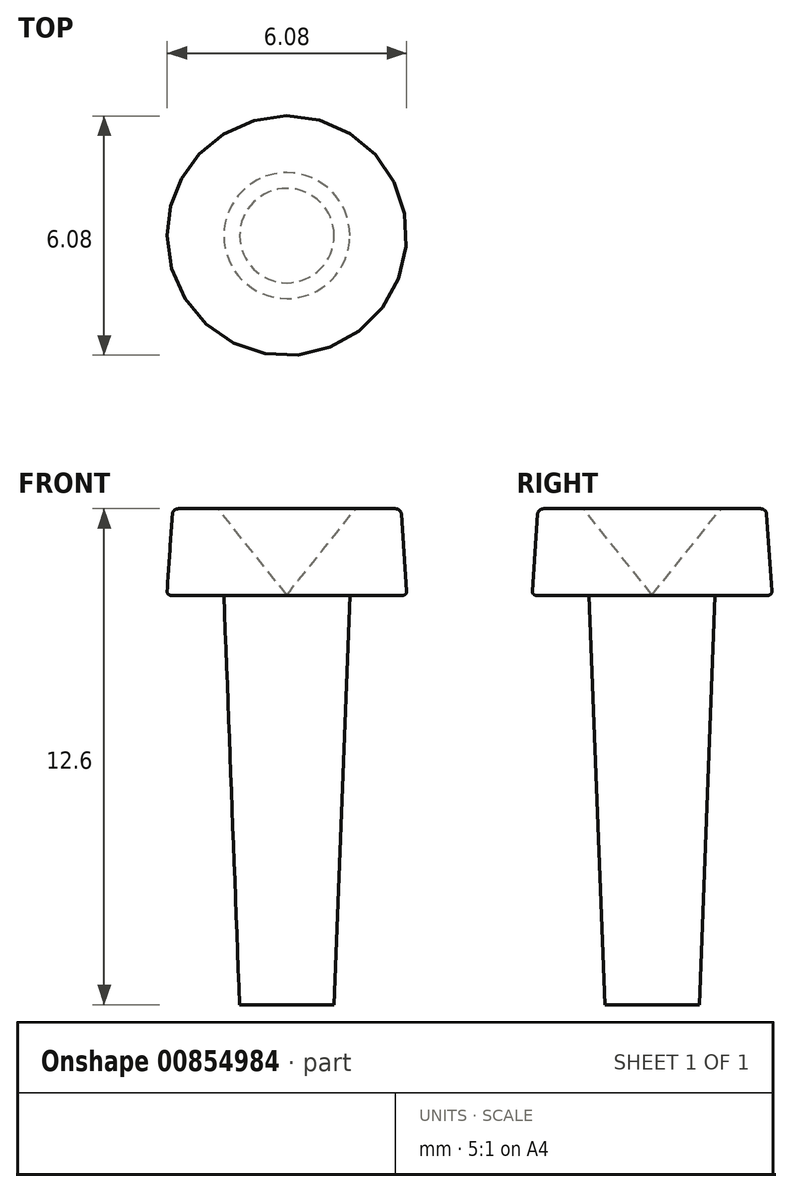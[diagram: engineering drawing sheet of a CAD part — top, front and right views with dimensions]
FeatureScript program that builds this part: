
annotation { "Feature Type Name" : "Feature", "Feature Type Description" : "" }
export const myFeature = defineFeature(function(context is Context, id is Id, definition is map)
    precondition{}
    {
        {
            var Q0;
            Q0=qCreatedBy(makeId("Front.planeOp"),FACE);
            var sketch = newSketch(context, id + "F0", { "sketchPlane" : qUnion([Q0])});
            skLineSegment(sketch, "E0", {"start": v(0, 7.12) * mm, "end": v(0, -15.42) * mm});
            skLineSegment(sketch, "E1", {"start": v(0, 0) * mm, "end": v(2.94, 0) * mm});
            skLineSegment(sketch, "E2", {"start": v(3.04, 0.1) * mm, "end": v(2.9, 2.06) * mm});
            skLineSegment(sketch, "E3", {"start": v(2.76, 2.2) * mm, "end": v(1.8, 2.2) * mm});
            skLineSegment(sketch, "E4", {"start": v(1.72, 2.16) * mm, "end": v(0, 0) * mm});
            skLineSegment(sketch, "E5", {"start": v(0, 0) * mm, "end": v(0, 0) * mm});
            skLineSegment(sketch, "E6", {"start": v(1.84, 2.2) * mm, "end": v(1.84, 0) * mm, "construction": true});
            skLineSegment(sketch, "E7", {"start": v(1.64, 2.2) * mm, "end": v(-0.81, 2.2) * mm, "construction": true});
            skLineSegment(sketch, "E8", {"start": v(0, 0.01) * mm, "end": v(-0.66, 0) * mm, "construction": true});
            skLineSegment(sketch, "E9", {"start": v(0, 0) * mm, "end": v(0, -10.4) * mm});
            skLineSegment(sketch, "E10", {"start": v(0, -10.4) * mm, "end": v(0, 0) * mm});
            skLineSegment(sketch, "E11", {"start": v(0, -10.4) * mm, "end": v(1.2, -10.4) * mm});
            skLineSegment(sketch, "E12", {"start": v(1.2, -10.4) * mm, "end": v(1.6, 0) * mm});
            skPoint(sketch, "E13.visualSharp", {"position": v(2.9, 2.2) * mm});
            skArc(sketch, "E13.filletArc", {"start": v(2.9, 2.06) * mm, "mid": v(2.86, 2.16) * mm, "end": v(2.76, 2.2) * mm});
            skPoint(sketch, "E14.visualSharp", {"position": v(1.75, 2.2) * mm});
            skArc(sketch, "E14.filletArc", {"start": v(1.8, 2.2) * mm, "mid": v(1.75, 2.2) * mm, "end": v(1.72, 2.16) * mm});
            skPoint(sketch, "E15.visualSharp", {"position": v(3.05, 0) * mm});
            skArc(sketch, "E15.filletArc", {"start": v(2.94, 0) * mm, "mid": v(3.02, 0.03) * mm, "end": v(3.04, 0.1) * mm});
            skSolve(sketch);
        }
        {
            var Q0;
            Q0 = qSketchRegion(id + "F0", true);
            var Q1;
            Q1=sQuery(id+"F0.wireOp",EDGE,"E10");
            revolve(context, id + "F1", {"surfaceOperationType" : NewSurfaceOperationType.NEW, "entities" : qUnion([Q0]), "axis" : qUnion([Q1]), "revolveType" : RevolveType.FULL});
        }
    });
